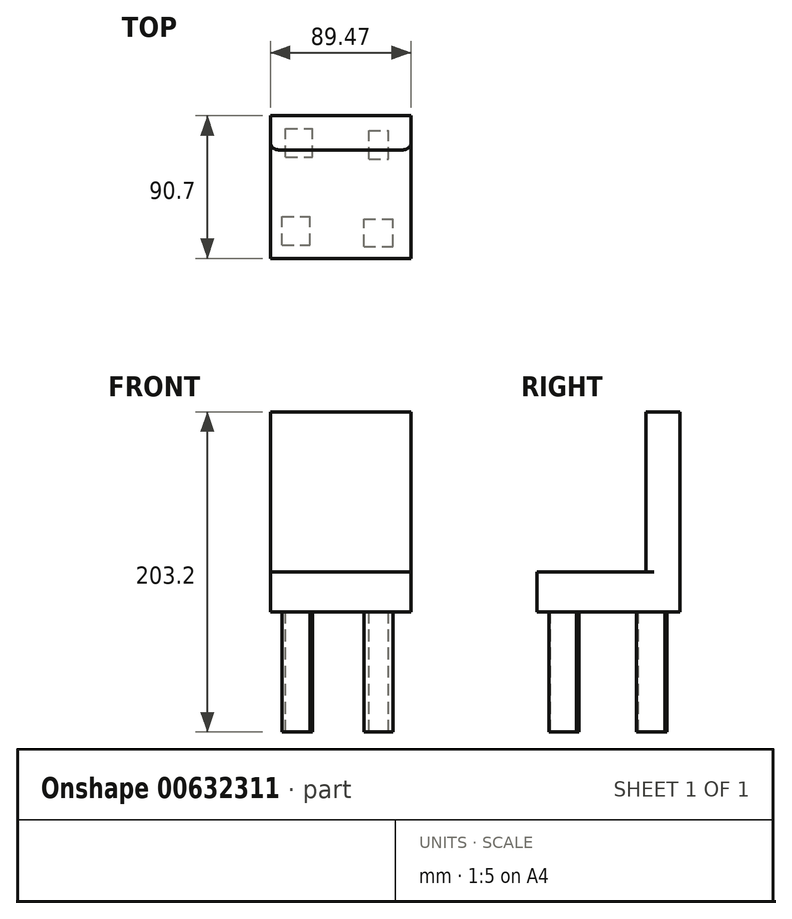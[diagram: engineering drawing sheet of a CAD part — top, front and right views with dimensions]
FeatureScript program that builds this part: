
annotation { "Feature Type Name" : "Feature", "Feature Type Description" : "" }
export const myFeature = defineFeature(function(context is Context, id is Id, definition is map)
    precondition{}
    {
        {
            var Q0;
            Q0=qCreatedBy(makeId("Top.planeOp"),FACE);
            var sketch = newSketch(context, id + "F0", { "sketchPlane" : qUnion([Q0])});
            skLineSegment(sketch, "E0.bottom", {"start": v(-55, 38.17) * mm, "end": v(34.47, 38.17) * mm});
            skLineSegment(sketch, "E0.top", {"start": v(-55, -52.53) * mm, "end": v(34.47, -52.53) * mm});
            skLineSegment(sketch, "E0.left", {"start": v(-55, 38.17) * mm, "end": v(-55, -52.53) * mm});
            skLineSegment(sketch, "E0.right", {"start": v(34.47, 38.17) * mm, "end": v(34.47, -52.53) * mm});
            skSolve(sketch);
        }
        {
            var Q0;
            Q0=makeQuery(id+"F0.imprint","IMPRINT",FACE,{"disambiguationData":[TD([[makeQuery(id+"F0.imprint","IMPRINT",EDGE,{"derivedFrom":sQuery(id+"F0.wireOp",EDGE,"E0.bottom")}),-1.0]])]});
            extrude(context, id + "F1", {"entities" : qUnion([Q0]), "depth" : 25.4 * mm, "offsetDistance" : 25.4 * mm});
        }
        {
            var Q0;
            Q0=makeQuery(id+"F1.opExtrude","CAP_FACE",FACE,{"disambiguationData":[OSD([sQuery(id+"F0.wireOp",EDGE,"E0.bottom"),sQuery(id+"F0.wireOp",EDGE,"E0.top"),sQuery(id+"F0.wireOp",EDGE,"E0.left"),sQuery(id+"F0.wireOp",EDGE,"E0.right")])],"isStart":false});
            var sketch = newSketch(context, id + "F2", { "sketchPlane" : qUnion([Q0])});
            skLineSegment(sketch, "E1", {"start": v(-55, 16.45) * mm, "end": v(34.47, 16.45) * mm});
            skSolve(sketch);
        }
        {
            var Q0;
            {var subQ0=sQuery(id+"F2.wireOp",EDGE,"E1");Q0=makeQuery(id+"F2.imprint","IMPRINT",FACE,{"disambiguationData":[TD([[makeQuery(id+"F2.imprint","IMPRINT",EDGE,{"derivedFrom":subQ0}),1.0]])]});}
            extrude(context, id + "F3", {"entities" : qUnion([Q0]), "operationType" : NewBodyOperationType.ADD, "depth" : 101.6 * mm, "offsetDistance" : 25.4 * mm});
        }
        {
            var Q0;
            Q0=makeQuery(id+"F1.opExtrude","CAP_FACE",FACE,{"disambiguationData":[OSD([sQuery(id+"F0.wireOp",EDGE,"E0.bottom"),sQuery(id+"F0.wireOp",EDGE,"E0.top"),sQuery(id+"F0.wireOp",EDGE,"E0.left"),sQuery(id+"F0.wireOp",EDGE,"E0.right")])],"isStart":true});
            var sketch = newSketch(context, id + "F4", { "sketchPlane" : qUnion([Q0])});
            skLineSegment(sketch, "E2.bottom", {"start": v(-47.57, 44.09) * mm, "end": v(-29.85, 44.09) * mm});
            skLineSegment(sketch, "E2.top", {"start": v(-47.57, 25.98) * mm, "end": v(-29.85, 25.98) * mm});
            skLineSegment(sketch, "E2.left", {"start": v(-47.57, 44.09) * mm, "end": v(-47.57, 25.98) * mm});
            skLineSegment(sketch, "E2.right", {"start": v(-29.85, 44.09) * mm, "end": v(-29.85, 25.98) * mm});
            skLineSegment(sketch, "E3.bottom", {"start": v(4.4, 44.87) * mm, "end": v(22.9, 44.87) * mm});
            skLineSegment(sketch, "E3.top", {"start": v(4.4, 27.55) * mm, "end": v(22.9, 27.55) * mm});
            skLineSegment(sketch, "E3.left", {"start": v(4.4, 44.87) * mm, "end": v(4.4, 27.55) * mm});
            skLineSegment(sketch, "E3.right", {"start": v(22.9, 44.87) * mm, "end": v(22.9, 27.55) * mm});
            skLineSegment(sketch, "E4.bottom", {"start": v(-45.2, -11.81) * mm, "end": v(-28.28, -11.81) * mm});
            skLineSegment(sketch, "E4.top", {"start": v(-45.2, -29.92) * mm, "end": v(-28.28, -29.92) * mm});
            skLineSegment(sketch, "E4.left", {"start": v(-45.2, -11.81) * mm, "end": v(-45.2, -29.92) * mm});
            skLineSegment(sketch, "E4.right", {"start": v(-28.28, -11.81) * mm, "end": v(-28.28, -29.92) * mm});
            skLineSegment(sketch, "E5.bottom", {"start": v(7.55, -10.63) * mm, "end": v(20.14, -10.63) * mm});
            skLineSegment(sketch, "E5.top", {"start": v(7.55, -28.74) * mm, "end": v(20.14, -28.74) * mm});
            skLineSegment(sketch, "E5.left", {"start": v(7.55, -10.63) * mm, "end": v(7.55, -28.74) * mm});
            skLineSegment(sketch, "E5.right", {"start": v(20.14, -10.63) * mm, "end": v(20.14, -28.74) * mm});
            skSolve(sketch);
        }
        {
            var Q0;
            Q0=makeQuery(id+"F4.imprint","IMPRINT",FACE,{"disambiguationData":[TD([[makeQuery(id+"F4.imprint","IMPRINT",EDGE,{"derivedFrom":sQuery(id+"F4.wireOp",EDGE,"E2.bottom")}),-1.0]])]});
            var Q1;
            Q1=makeQuery(id+"F4.imprint","IMPRINT",FACE,{"disambiguationData":[TD([[makeQuery(id+"F4.imprint","IMPRINT",EDGE,{"derivedFrom":sQuery(id+"F4.wireOp",EDGE,"E3.bottom")}),-1.0]])]});
            var Q2;
            Q2=makeQuery(id+"F4.imprint","IMPRINT",FACE,{"disambiguationData":[TD([[makeQuery(id+"F4.imprint","IMPRINT",EDGE,{"derivedFrom":sQuery(id+"F4.wireOp",EDGE,"E5.bottom")}),-1.0]])]});
            var Q3;
            Q3=makeQuery(id+"F4.imprint","IMPRINT",FACE,{"disambiguationData":[TD([[makeQuery(id+"F4.imprint","IMPRINT",EDGE,{"derivedFrom":sQuery(id+"F4.wireOp",EDGE,"E4.bottom")}),-1.0]])]});
            extrude(context, id + "F5", {"entities" : qUnion([Q0, Q1, Q2, Q3]), "operationType" : NewBodyOperationType.ADD, "depth" : 76.2 * mm, "offsetDistance" : 25.4 * mm});
        }
        {
            var Q0;
            Q0=makeQuery(id+"F3.opExtrude","SWEPT_EDGE",EDGE,{"disambiguationData":[OSD([sQuery(id+"F0.wireOp",EDGE,"E0.right"),sQuery(id+"F2.wireOp",EDGE,"E1")])]});
            var Q1;
            Q1=makeQuery(id+"F3.opExtrude","SWEPT_EDGE",EDGE,{"disambiguationData":[OSD([sQuery(id+"F0.wireOp",EDGE,"E0.left"),sQuery(id+"F2.wireOp",EDGE,"E1")])]});
            fillet(context, id + "F6", {"entities" : qUnion([Q0, Q1]), "radius" : 5.08 * mm, "tangentPropagation" : true, "allowEdgeOverflow" : false});
        }
    });
